# Revit family: ledspotra-chiara-e_8w-827-36d-al_541003411200
name_source: partatom
category: Leuchten
revit_build: Autodesk Revit 2016 (Build: 20190508_0715(x64)
units: mm (PartAtom-declared; Revit-internal decimal feet)

## family parameters
Basisbauteil = Fläche
Beim Laden mit Abzugskörper schneiden = Nein
Bemaßung runder Anschluss = Durchmesser verwenden
Gemeinsam genutzt = Nein
Lichtquelle = Nein
Raumberechnungspunkt = Nein
Teiletyp = Normal

## types (1)
- LEDSpotRA-Chiara-E 8W-827-36D-AL (1 x LED, 620 lm)
    Approval mark = CE
    Beschreibung = Recessed LED spot with 25° tilting angle. Clean beam thanks to newly designed micro faceted reflector. Light free of multiple shadows for professional accent lighting. Universal cut-out of 68mm. IP44 on the light emitting side.
    CIE Flux Codes = 95 98 100 99 100
    Control Gear = Electronic ballast
    Height = 0 mm  [stored 0 ft]
    Hersteller = OPPLE
    Lamp Light Flux = 620 lm
    Lamp count = 1
    Lampe = 1 x LED
    Length = 85 mm
    Luminous efficacy = 78 lm/W
    ModVariant = Nein
    Modell = 541003411200
    Mounting Place = Ceiling
    Mounting Type = Recessed
    Number of Poles = 1
    OnlyDefault = Ja
    Power Factor = 1
    Product Name = LEDSpotRA-Chiara-E 8W-827-36D-AL
    Product group = Spot Chiara
    ProductGroupID = 430
    Protection Class = Protection class II
    Protection Degree = IP 44
    RLX_Detail_Level = 1
    RlxData = <blob elided: 25701 chars, md5=b3712621>
    Scheinlast = 8 VA
    Socket = socket
    Standby Power = 0 W
    System Light Flux = 620 lm
    System Power = 8 W
    Typenbild = 541003411200.jpg
    Typenkommentare = Product without accessories
    URL = http://relux.com
    VarID = ---
    Voltage = 0 V
    Vorgabe-Ansicht = 1800 mm
    Weight = 0.00 kg
    Width = 0 mm  [stored 0 ft]

note: [stored X ft] marks values corroborated as IEEE doubles in the binary element streams (Revit-internal decimal feet)

## geometry (parser evidence)
native form markers: Blend x4, Sweep x11
no freeform markers — native parametric forms only
